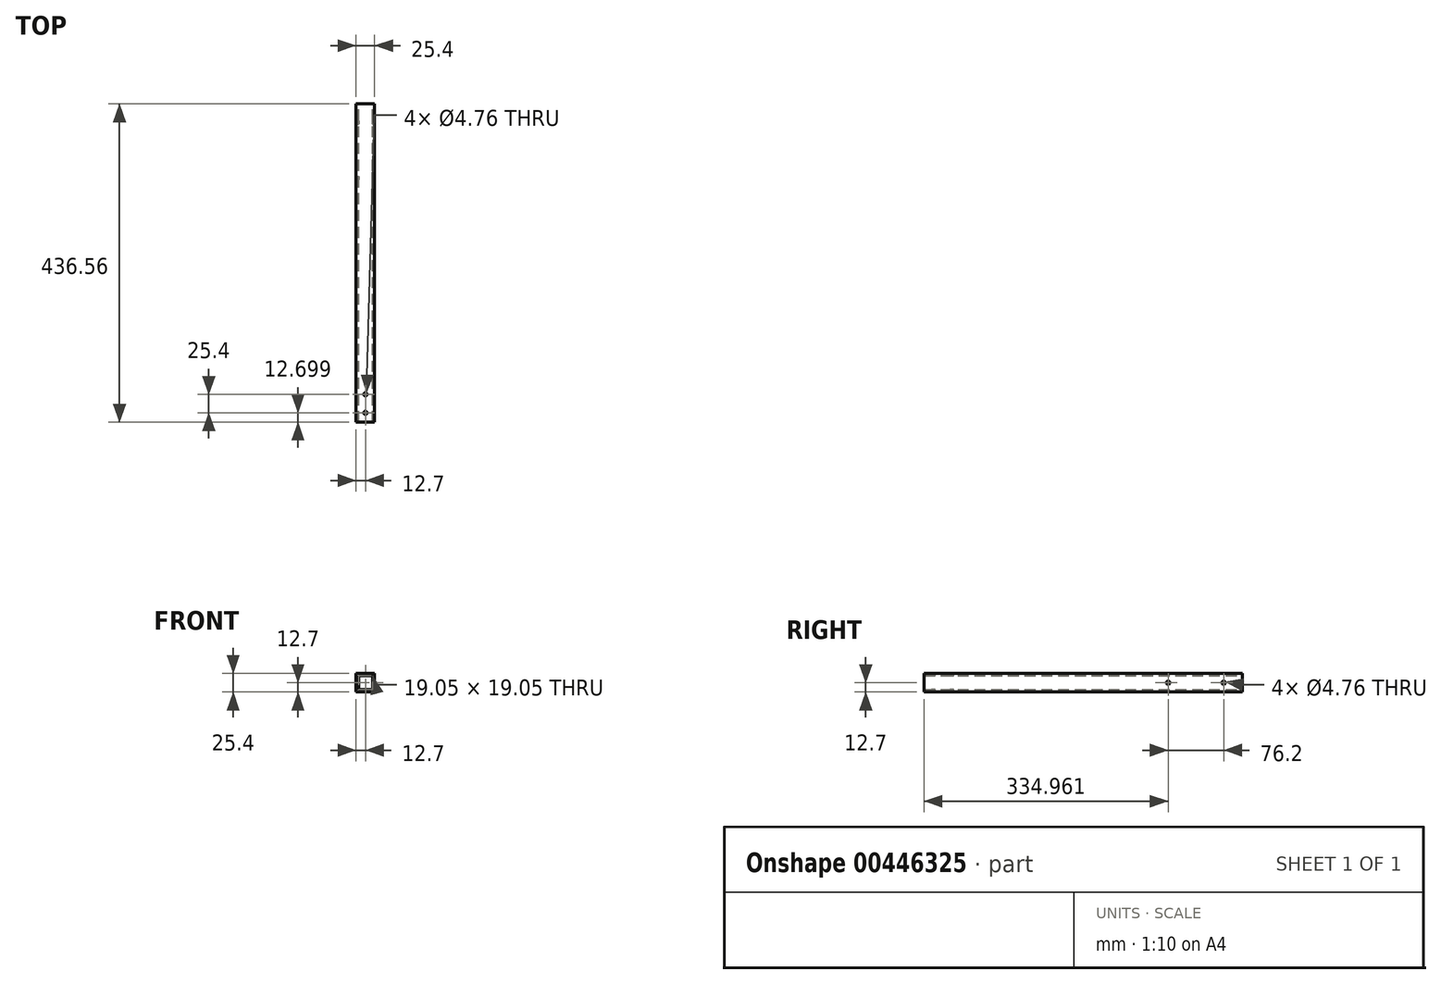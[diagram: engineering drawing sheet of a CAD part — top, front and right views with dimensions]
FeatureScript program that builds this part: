
annotation { "Feature Type Name" : "Feature", "Feature Type Description" : "" }
export const myFeature = defineFeature(function(context is Context, id is Id, definition is map)
    precondition{}
    {
        {
            var Q0;
            Q0=qCreatedBy(makeId("Front.planeOp"),FACE);
            var sketch = newSketch(context, id + "F0", { "sketchPlane" : qUnion([Q0])});
            skLineSegment(sketch, "E0.bottom", {"start": v(12.7, 12.7) * mm, "end": v(-12.7, 12.7) * mm});
            skLineSegment(sketch, "E0.top", {"start": v(12.7, -12.7) * mm, "end": v(-12.7, -12.7) * mm});
            skLineSegment(sketch, "E0.left", {"start": v(12.7, 12.7) * mm, "end": v(12.7, -12.7) * mm});
            skLineSegment(sketch, "E0.right", {"start": v(-12.7, 12.7) * mm, "end": v(-12.7, -12.7) * mm});
            skPoint(sketch, "E0.middle", {"position": v(0, 0) * mm});
            skLineSegment(sketch, "E1.0", {"start": v(9.52, 9.53) * mm, "end": v(-9.53, 9.53) * mm});
            skLineSegment(sketch, "E1.1", {"start": v(9.52, 9.53) * mm, "end": v(9.53, -9.53) * mm});
            skLineSegment(sketch, "E1.2", {"start": v(9.52, -9.53) * mm, "end": v(-9.53, -9.53) * mm});
            skLineSegment(sketch, "E1.3", {"start": v(-9.53, 9.53) * mm, "end": v(-9.53, -9.53) * mm});
            skSolve(sketch);
        }
        {
            var Q0;
            Q0=makeQuery(id+"F0.imprint","IMPRINT",FACE,{"disambiguationData":[TD([[makeQuery(id+"F0.imprint","IMPRINT",EDGE,{"derivedFrom":sQuery(id+"F0.wireOp",EDGE,"E0.bottom")}),1.0]])]});
            extrude(context, id + "F1", {"entities" : qUnion([Q0]), "depth" : 436.56 * mm, "offsetDistance" : 25.4 * mm, "symmetric" : true});
        }
        {
            var Q0;
            Q0=makeQuery(id+"F1.opExtrude","SWEPT_FACE",FACE,{"disambiguationData":[OSD([sQuery(id+"F0.wireOp",EDGE,"E0.bottom")])]});
            var sketch = newSketch(context, id + "F2", { "sketchPlane" : qUnion([Q0])});
            skLineSegment(sketch, "E2", {"start": v(0, -218.28) * mm, "end": v(0, -116.32) * mm, "construction": true});
            skCircle(sketch, "E3", {"center": v(0, -205.58) * mm, "radius": 2.38 * mm});
            skCircle(sketch, "E4", {"center": v(0, -180.18) * mm, "radius": 2.38 * mm});
            skSolve(sketch);
        }
        {
            var Q0;
            Q0=makeQuery(id+"F2.imprint","IMPRINT",FACE,{"disambiguationData":[TD([[makeQuery(id+"F2.imprint","IMPRINT",EDGE,{"derivedFrom":sQuery(id+"F2.wireOp",EDGE,"E3")}),1.0]])]});
            var Q1;
            Q1=makeQuery(id+"F2.imprint","IMPRINT",FACE,{"disambiguationData":[TD([[makeQuery(id+"F2.imprint","IMPRINT",EDGE,{"derivedFrom":sQuery(id+"F2.wireOp",EDGE,"E4")}),1.0]])]});
            extrude(context, id + "F3", {"entities" : qUnion([Q0, Q1]), "operationType" : NewBodyOperationType.REMOVE, "endBound" : BoundingType.THROUGH_ALL, "oppositeDirection" : true, "depth" : 25.4 * mm, "offsetDistance" : 25.4 * mm});
        }
        {
            var Q0;
            Q0=makeQuery(id+"F1.opExtrude","SWEPT_FACE",FACE,{"disambiguationData":[OSD([sQuery(id+"F0.wireOp",EDGE,"E0.left")])]});
            var sketch = newSketch(context, id + "F4", { "sketchPlane" : qUnion([Q0])});
            skLineSegment(sketch, "E5", {"start": v(218.28, 0) * mm, "end": v(116.68, 0) * mm, "construction": true});
            skPoint(sketch, "E5.endSnap0", {"position": v(218.28, 0) * mm});
            skCircle(sketch, "E6", {"center": v(192.88, 0) * mm, "radius": 2.38 * mm});
            skCircle(sketch, "E7", {"center": v(116.68, 0) * mm, "radius": 2.38 * mm});
            skSolve(sketch);
        }
        {
            var Q0;
            Q0 = qSketchRegion(id + "F4", true);
            extrude(context, id + "F5", {"entities" : qUnion([Q0]), "operationType" : NewBodyOperationType.REMOVE, "endBound" : BoundingType.THROUGH_ALL, "oppositeDirection" : true, "depth" : 25.4 * mm, "offsetDistance" : 25.4 * mm});
        }
    });
